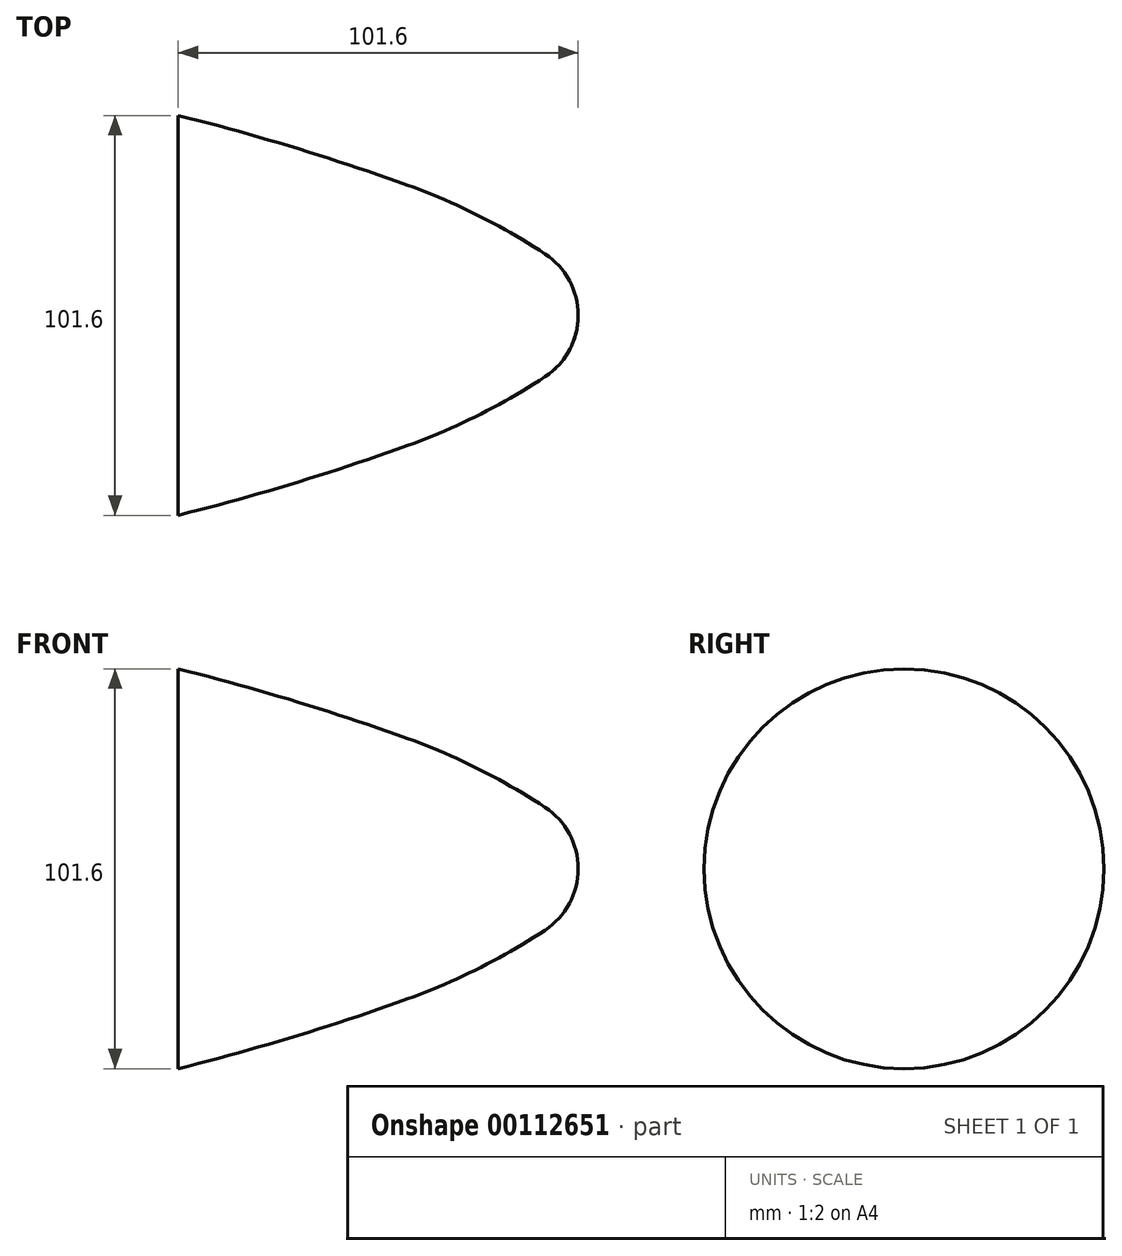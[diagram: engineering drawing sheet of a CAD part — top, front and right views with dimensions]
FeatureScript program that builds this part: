
annotation { "Feature Type Name" : "Feature", "Feature Type Description" : "" }
export const myFeature = defineFeature(function(context is Context, id is Id, definition is map)
    precondition{}
    {
        {
            var Q0;
            Q0=qCreatedBy(makeId("Top.planeOp"),FACE);
            var sketch = newSketch(context, id + "F0", { "sketchPlane" : qUnion([Q0])});
            skLineSegment(sketch, "E0", {"start": v(0, 0) * mm, "end": v(-25.4, 0) * mm, "construction": true});
            skLineSegment(sketch, "E1", {"start": v(0, 0) * mm, "end": v(0, -25.4) * mm, "construction": true});
            skLineSegment(sketch, "E2", {"start": v(0, -25.4) * mm, "end": v(-25.4, -25.4) * mm, "construction": true});
            skLineSegment(sketch, "E3", {"start": v(-25.4, 0) * mm, "end": v(-25.4, -25.4) * mm, "construction": true});
            skArc(sketch, "E4", {"start": v(-8.41, -15.61) * mm, "mid": v(-2.24, -8.87) * mm, "end": v(0, 0) * mm});
            skLineSegment(sketch, "E5", {"start": v(0, 0) * mm, "end": v(-25.4, -25.4) * mm, "construction": true});
            skLineSegment(sketch, "E6", {"start": v(-25.4, -25.4) * mm, "end": v(-50.8, -25.4) * mm, "construction": true});
            skLineSegment(sketch, "E7", {"start": v(-50.8, -25.4) * mm, "end": v(-76.2, -25.4) * mm, "construction": true});
            skLineSegment(sketch, "E8", {"start": v(-76.2, -25.4) * mm, "end": v(-76.2, -50.8) * mm, "construction": true});
            skLineSegment(sketch, "E9", {"start": v(-25.4, -25.4) * mm, "end": v(-76.2, -50.8) * mm, "construction": true});
            skLineSegment(sketch, "E10", {"start": v(0, -25.4) * mm, "end": v(0, -50.8) * mm, "construction": true});
            skLineSegment(sketch, "E11", {"start": v(0, -50.8) * mm, "end": v(-25.4, -50.8) * mm, "construction": true});
            skLineSegment(sketch, "E12", {"start": v(-25.4, -25.4) * mm, "end": v(-25.4, -50.8) * mm, "construction": true});
            skLineSegment(sketch, "E13", {"start": v(-76.2, -25.4) * mm, "end": v(-101.6, -25.4) * mm, "construction": true});
            skLineSegment(sketch, "E14", {"start": v(-101.6, -25.4) * mm, "end": v(-101.6, -50.8) * mm, "construction": true});
            skLineSegment(sketch, "E15", {"start": v(-76.2, -50.8) * mm, "end": v(-50.8, -50.8) * mm, "construction": true});
            skLineSegment(sketch, "E16", {"start": v(-50.8, -50.8) * mm, "end": v(-25.4, -50.8) * mm, "construction": true});
            skLineSegment(sketch, "E17", {"start": v(-76.2, -50.8) * mm, "end": v(-101.6, -50.8) * mm, "construction": true});
            skLineSegment(sketch, "E18", {"start": v(-101.6, -50.8) * mm, "end": v(-127, -50.8) * mm, "construction": true});
            skLineSegment(sketch, "E19", {"start": v(-127, -50.8) * mm, "end": v(-152.4, -50.8) * mm, "construction": true});
            skLineSegment(sketch, "E20", {"start": v(-152.4, -50.8) * mm, "end": v(-177.8, -50.8) * mm, "construction": true});
            skLineSegment(sketch, "E21", {"start": v(-177.8, -50.8) * mm, "end": v(-203.2, -50.8) * mm, "construction": true});
            skLineSegment(sketch, "E22", {"start": v(-203.2, -50.8) * mm, "end": v(-203.2, -76.2) * mm, "construction": true});
            skLineSegment(sketch, "E23", {"start": v(-101.6, -50.8) * mm, "end": v(-203.2, -76.2) * mm, "construction": true});
            skArc(sketch, "E24", {"start": v(-101.6, -50.8) * mm, "mid": v(-72.29, -42.69) * mm, "end": v(-43.42, -33.11) * mm});
            skArc(sketch, "E25", {"start": v(-43.42, -33.11) * mm, "mid": v(-25.4, -25.4) * mm, "end": v(-8.41, -15.61) * mm});
            skLineSegment(sketch, "E26", {"start": v(0, 0) * mm, "end": v(-101.6, 0) * mm});
            skLineSegment(sketch, "E27", {"start": v(-101.6, -50.8) * mm, "end": v(-101.6, 0) * mm});
            skSolve(sketch);
        }
        {
            var Q0;
            Q0=qCreatedBy(makeId("Right.planeOp"),FACE);
            var sketch = newSketch(context, id + "F1", { "sketchPlane" : qUnion([Q0])});
            skCircle(sketch, "E28", {"center": v(0, 0) * mm, "radius": 12.7 * mm});
            skSolve(sketch);
        }
        {
            var Q0;
            Q0=makeQuery(id+"F0.imprint","IMPRINT",FACE,{"disambiguationData":[TD([[makeQuery(id+"F0.imprint","IMPRINT",EDGE,{"derivedFrom":sQuery(id+"F0.wireOp",EDGE,"E4")}),1.0]])]});
            var Q1;
            Q1=sQuery(id+"F1.wireOp",EDGE,"E28");
            revolve(context, id + "F2", {"entities" : qUnion([Q0]), "axis" : qUnion([Q1]), "revolveType" : RevolveType.FULL});
        }
    });
